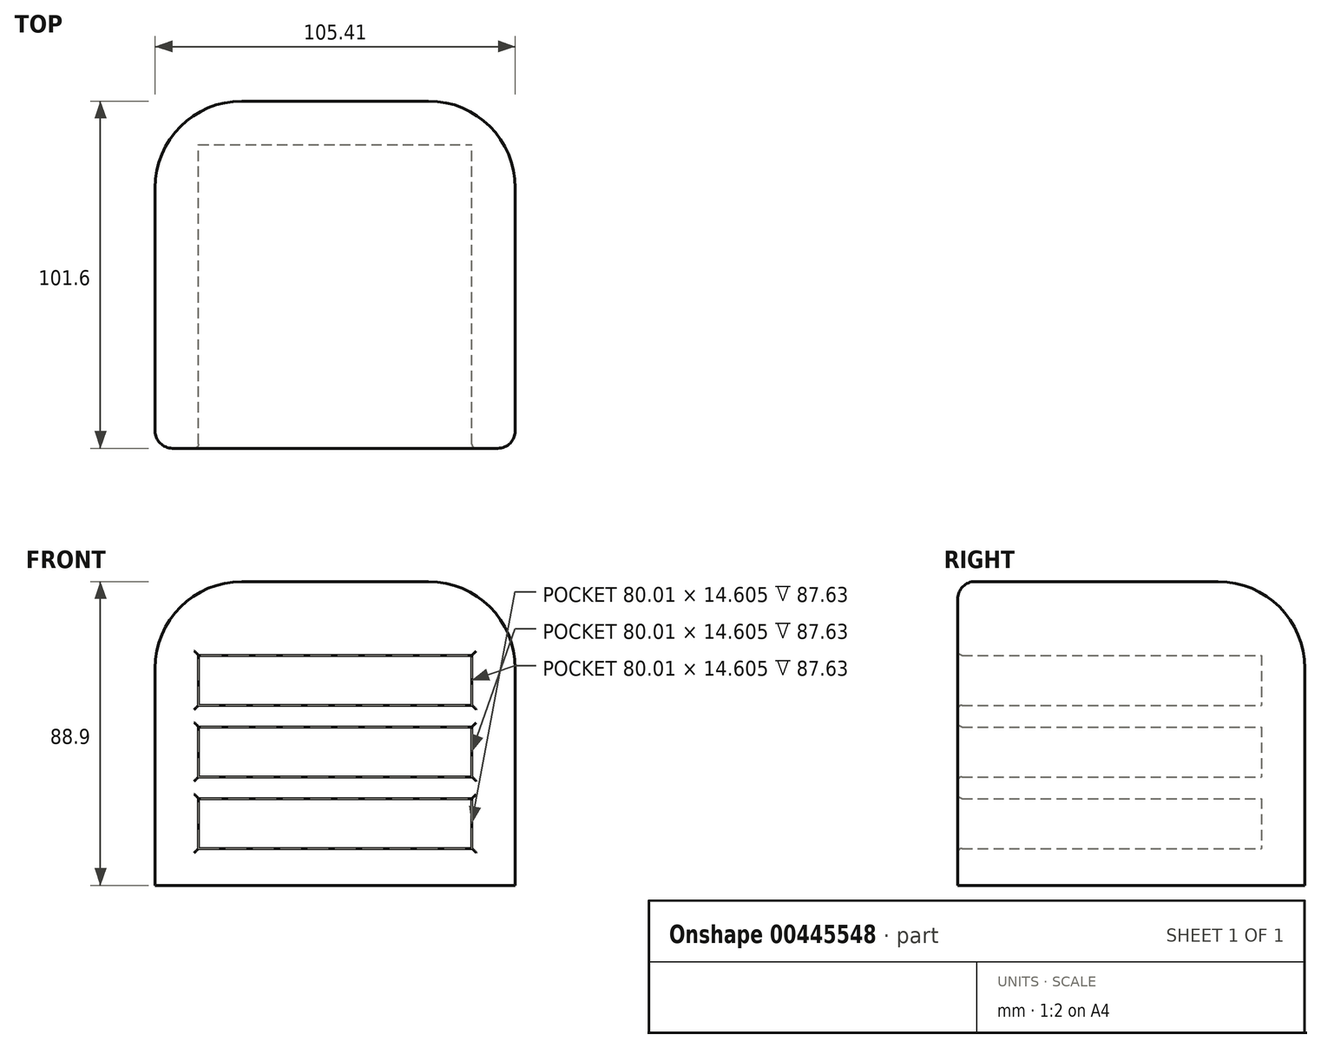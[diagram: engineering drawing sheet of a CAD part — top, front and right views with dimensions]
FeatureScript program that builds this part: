
annotation { "Feature Type Name" : "Feature", "Feature Type Description" : "" }
export const myFeature = defineFeature(function(context is Context, id is Id, definition is map)
    precondition{}
    {
        {
            var Q0;
            Q0=qCreatedBy(makeId("Front.planeOp"),FACE);
            var sketch = newSketch(context, id + "F0", { "sketchPlane" : qUnion([Q0])});
            skLineSegment(sketch, "E0.bottom", {"start": v(-40, 25.4) * mm, "end": v(40, 25.4) * mm});
            skLineSegment(sketch, "E0.top", {"start": v(-40, 10.8) * mm, "end": v(40, 10.8) * mm});
            skLineSegment(sketch, "E0.left", {"start": v(-40, 25.4) * mm, "end": v(-40, 10.8) * mm});
            skLineSegment(sketch, "E0.right", {"start": v(40, 25.4) * mm, "end": v(40, 10.8) * mm});
            skPoint(sketch, "E1", {"position": v(0, 25.4) * mm});
            skLineSegment(sketch, "E2.bottom", {"start": v(-40, 46.36) * mm, "end": v(40, 46.36) * mm});
            skLineSegment(sketch, "E2.top", {"start": v(-40, 31.75) * mm, "end": v(40, 31.75) * mm});
            skLineSegment(sketch, "E2.left", {"start": v(-40, 46.35) * mm, "end": v(-40, 31.75) * mm});
            skLineSegment(sketch, "E2.right", {"start": v(40, 46.36) * mm, "end": v(40, 31.75) * mm});
            skPoint(sketch, "E3", {"position": v(0, 31.75) * mm});
            skPoint(sketch, "E4", {"position": v(0, 46.36) * mm});
            skPoint(sketch, "E5", {"position": v(0, 52.7) * mm});
            skLineSegment(sketch, "E6.bottom", {"start": v(-40, 67.31) * mm, "end": v(40, 67.3) * mm});
            skLineSegment(sketch, "E6.top", {"start": v(-40, 52.7) * mm, "end": v(40, 52.7) * mm});
            skLineSegment(sketch, "E6.left", {"start": v(-40, 67.31) * mm, "end": v(-40, 52.7) * mm});
            skLineSegment(sketch, "E6.right", {"start": v(40, 67.31) * mm, "end": v(40, 52.7) * mm});
            skLineSegment(sketch, "E7.bottom", {"start": v(-52.7, 0) * mm, "end": v(52.7, 0) * mm});
            skLineSegment(sketch, "E7.top", {"start": v(-52.7, 88.9) * mm, "end": v(52.7, 88.9) * mm});
            skLineSegment(sketch, "E7.left", {"start": v(-52.7, 0) * mm, "end": v(-52.7, 88.9) * mm});
            skLineSegment(sketch, "E7.right", {"start": v(52.7, 0) * mm, "end": v(52.7, 88.9) * mm});
            skSolve(sketch);
        }
        {
            var Q0;
            Q0 = qSketchRegion(id + "F0", true);
            extrude(context, id + "F1", {"entities" : qUnion([Q0]), "depth" : 101.6 * mm});
        }
        {
            var Q0;
            Q0=makeQuery(id+"F1.opExtrude","SWEPT_EDGE",EDGE,{"disambiguationData":[OSD([sQuery(id+"F0.wireOp",EDGE,"E7.top"),sQuery(id+"F0.wireOp",EDGE,"E7.left")])]});
            var Q1;
            Q1=makeQuery(id+"F1.opExtrude","SWEPT_EDGE",EDGE,{"disambiguationData":[OSD([sQuery(id+"F0.wireOp",EDGE,"E7.top"),sQuery(id+"F0.wireOp",EDGE,"E7.right")])]});
            fillet(context, id + "F2", {"entities" : qUnion([Q0, Q1]), "radius" : 25.4 * mm, "tangentPropagation" : true, "allowEdgeOverflow" : false});
        }
        {
            var Q0;
            Q0=makeQuery(id+"F1.opExtrude","CAP_EDGE",EDGE,{"disambiguationData":[OSD([sQuery(id+"F0.wireOp",EDGE,"E6.bottom")])],"isStart":false});
            var Q1;
            Q1=makeQuery(id+"F1.opExtrude","CAP_EDGE",EDGE,{"disambiguationData":[OSD([sQuery(id+"F0.wireOp",EDGE,"E6.left")])],"isStart":false});
            var Q2;
            Q2=makeQuery(id+"F1.opExtrude","CAP_EDGE",EDGE,{"disambiguationData":[OSD([sQuery(id+"F0.wireOp",EDGE,"E6.top")])],"isStart":false});
            var Q3;
            Q3=makeQuery(id+"F1.opExtrude","CAP_EDGE",EDGE,{"disambiguationData":[OSD([sQuery(id+"F0.wireOp",EDGE,"E6.right")])],"isStart":false});
            var Q4;
            Q4=makeQuery(id+"F1.opExtrude","CAP_EDGE",EDGE,{"disambiguationData":[OSD([sQuery(id+"F0.wireOp",EDGE,"E2.bottom")])],"isStart":false});
            var Q5;
            Q5=makeQuery(id+"F1.opExtrude","CAP_EDGE",EDGE,{"disambiguationData":[OSD([sQuery(id+"F0.wireOp",EDGE,"E2.left")])],"isStart":false});
            var Q6;
            Q6=makeQuery(id+"F1.opExtrude","CAP_EDGE",EDGE,{"disambiguationData":[OSD([sQuery(id+"F0.wireOp",EDGE,"E2.top")])],"isStart":false});
            var Q7;
            Q7=makeQuery(id+"F1.opExtrude","CAP_EDGE",EDGE,{"disambiguationData":[OSD([sQuery(id+"F0.wireOp",EDGE,"E2.right")])],"isStart":false});
            var Q8;
            Q8=makeQuery(id+"F1.opExtrude","CAP_EDGE",EDGE,{"disambiguationData":[OSD([sQuery(id+"F0.wireOp",EDGE,"E0.bottom")])],"isStart":false});
            var Q9;
            Q9=makeQuery(id+"F1.opExtrude","CAP_EDGE",EDGE,{"disambiguationData":[OSD([sQuery(id+"F0.wireOp",EDGE,"E0.left")])],"isStart":false});
            var Q10;
            Q10=makeQuery(id+"F1.opExtrude","CAP_EDGE",EDGE,{"disambiguationData":[OSD([sQuery(id+"F0.wireOp",EDGE,"E0.right")])],"isStart":false});
            var Q11;
            Q11=makeQuery(id+"F1.opExtrude","CAP_EDGE",EDGE,{"disambiguationData":[OSD([sQuery(id+"F0.wireOp",EDGE,"E0.top")])],"isStart":false});
            fillet(context, id + "F3", {"entities" : qUnion([Q0, Q1, Q2, Q3, Q4, Q5, Q6, Q7, Q8, Q9, Q10, Q11]), "radius" : 1.27 * mm, "tangentPropagation" : true, "allowEdgeOverflow" : false});
        }
        {
            var Q0;
            Q0=makeQuery(id+"F1.opExtrude","CAP_EDGE",EDGE,{"disambiguationData":[OSD([sQuery(id+"F0.wireOp",EDGE,"E7.top")])],"isStart":false});
            fillet(context, id + "F4", {"entities" : qUnion([Q0]), "radius" : 5.08 * mm, "tangentPropagation" : true, "allowEdgeOverflow" : false});
        }
        {
            var Q0;
            Q0=qCreatedBy(makeId("Front.planeOp"),FACE);
            var sketch = newSketch(context, id + "F5", { "sketchPlane" : qUnion([Q0])});
            skLineSegment(sketch, "E8.bottom", {"start": v(52.6, 0) * mm, "end": v(-52.81, 0) * mm});
            skLineSegment(sketch, "E8.top", {"start": v(52.6, 88.9) * mm, "end": v(-52.81, 88.9) * mm});
            skLineSegment(sketch, "E8.left", {"start": v(52.6, 0) * mm, "end": v(52.6, 88.9) * mm});
            skLineSegment(sketch, "E8.right", {"start": v(-52.81, 0) * mm, "end": v(-52.81, 88.9) * mm});
            skSolve(sketch);
        }
        {
            var Q0;
            Q0 = qSketchRegion(id + "F5", true);
            extrude(context, id + "F6", {"entities" : qUnion([Q0]), "operationType" : NewBodyOperationType.ADD, "depth" : 12.7 * mm});
        }
        {
            var Q0;
            Q0=makeQuery(id+"F6.opExtrude","SWEPT_EDGE",EDGE,{"disambiguationData":[OSD([sQuery(id+"F5.wireOp",EDGE,"E8.top"),sQuery(id+"F5.wireOp",EDGE,"E8.left")])]});
            var Q1;
            Q1=makeQuery(id+"F6.opExtrude","SWEPT_EDGE",EDGE,{"disambiguationData":[OSD([sQuery(id+"F5.wireOp",EDGE,"E8.top"),sQuery(id+"F5.wireOp",EDGE,"E8.right")])]});
            fillet(context, id + "F7", {"entities" : qUnion([Q0, Q1]), "radius" : 25.4 * mm, "tangentPropagation" : true, "allowEdgeOverflow" : false});
        }
        {
            var Q0;
            Q0=makeQuery(id+"F6.boolean.opBoolean","MERGE",EDGE,{"derivedFrom":[makeQuery(id+"F1.opExtrude","CAP_EDGE",EDGE,{"disambiguationData":[OSD([sQuery(id+"F0.wireOp",EDGE,"E7.top")])],"isStart":true}),makeQuery(id+"F6.opExtrude","CAP_EDGE",EDGE,{"disambiguationData":[OSD([sQuery(id+"F5.wireOp",EDGE,"E8.top")])],"isStart":true})]});
            fillet(context, id + "F8", {"entities" : qUnion([Q0]), "radius" : 25.4 * mm, "tangentPropagation" : true, "allowEdgeOverflow" : false});
        }
    });
